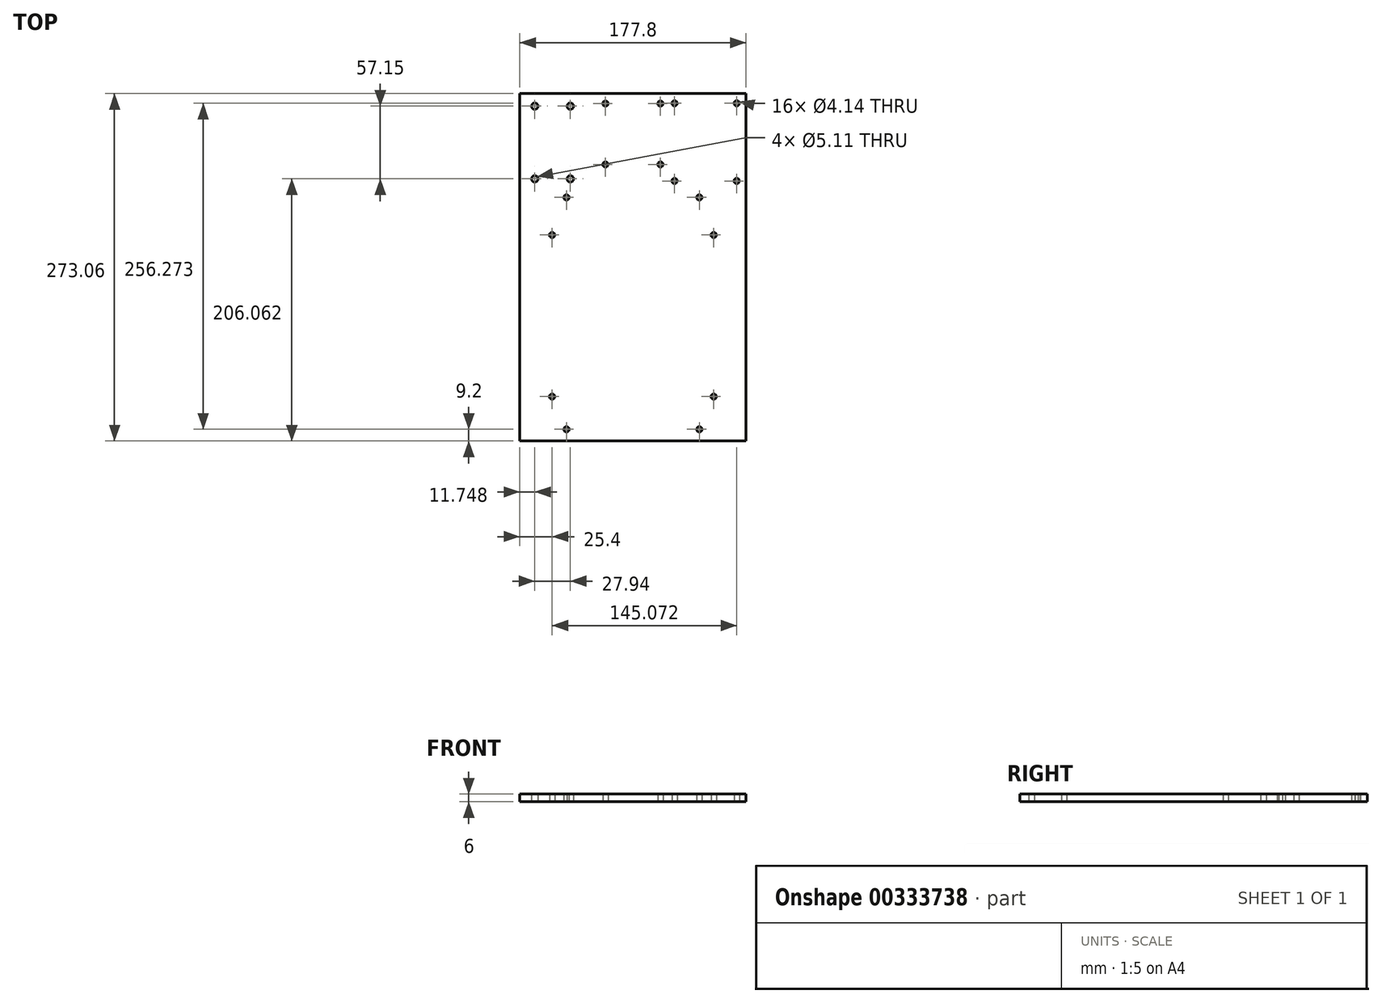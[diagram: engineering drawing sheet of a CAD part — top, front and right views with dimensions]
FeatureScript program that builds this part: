
annotation { "Feature Type Name" : "Feature", "Feature Type Description" : "" }
export const myFeature = defineFeature(function(context is Context, id is Id, definition is map)
    precondition{}
    {
        {
            var Q0;
            Q0=qCreatedBy(makeId("Top.planeOp"),FACE);
            var sketch = newSketch(context, id + "F0", { "sketchPlane" : qUnion([Q0])});
            skLineSegment(sketch, "E0.bottom", {"start": v(88.9, 136.52) * mm, "end": v(-88.9, 136.52) * mm});
            skLineSegment(sketch, "E0.top", {"start": v(88.9, -136.52) * mm, "end": v(-88.9, -136.52) * mm});
            skLineSegment(sketch, "E0.left", {"start": v(88.9, 136.52) * mm, "end": v(88.9, -136.52) * mm});
            skLineSegment(sketch, "E0.right", {"start": v(-88.9, 136.52) * mm, "end": v(-88.9, -136.52) * mm});
            skPoint(sketch, "E0.middle", {"position": v(0, 0) * mm});
            skLineSegment(sketch, "E1.bottom", {"start": v(71.59, 35.1) * mm, "end": v(-71.59, 35.1) * mm});
            skLineSegment(sketch, "E1.top", {"start": v(71.59, -111.3) * mm, "end": v(-71.59, -111.3) * mm, "construction": true});
            skLineSegment(sketch, "E1.left", {"start": v(71.59, 35.1) * mm, "end": v(71.59, -111.3) * mm, "construction": true});
            skLineSegment(sketch, "E1.right", {"start": v(-71.59, 35.1) * mm, "end": v(-71.59, -111.3) * mm, "construction": true});
            skPoint(sketch, "E1.middle", {"position": v(0, -38.1) * mm});
            skLineSegment(sketch, "E2.bottom", {"start": v(25.78, 76.58) * mm, "end": v(-25.78, 76.58) * mm});
            skLineSegment(sketch, "E2.top", {"start": v(25.78, 132.97) * mm, "end": v(-25.78, 132.97) * mm, "construction": true});
            skLineSegment(sketch, "E2.left", {"start": v(25.78, 76.58) * mm, "end": v(25.78, 132.97) * mm, "construction": true});
            skLineSegment(sketch, "E2.right", {"start": v(-25.78, 76.58) * mm, "end": v(-25.78, 132.97) * mm, "construction": true});
            skPoint(sketch, "E2.middle", {"position": v(0, 104.77) * mm});
            skLineSegment(sketch, "E3.bottom", {"start": v(21.62, 80.86) * mm, "end": v(-21.62, 80.86) * mm, "construction": true});
            skLineSegment(sketch, "E3.top", {"start": v(21.62, 128.69) * mm, "end": v(-21.62, 128.69) * mm, "construction": true});
            skLineSegment(sketch, "E3.left", {"start": v(21.62, 80.86) * mm, "end": v(21.62, 128.69) * mm, "construction": true});
            skLineSegment(sketch, "E3.right", {"start": v(-21.62, 80.86) * mm, "end": v(-21.62, 128.69) * mm, "construction": true});
            skLineSegment(sketch, "E4.bottom", {"start": v(85.55, 63.88) * mm, "end": v(28.75, 63.88) * mm, "construction": true});
            skLineSegment(sketch, "E4.top", {"start": v(85.55, 132.97) * mm, "end": v(28.75, 132.97) * mm, "construction": true});
            skLineSegment(sketch, "E4.left", {"start": v(85.55, 63.88) * mm, "end": v(85.55, 132.97) * mm, "construction": true});
            skLineSegment(sketch, "E4.right", {"start": v(28.75, 63.88) * mm, "end": v(28.75, 132.97) * mm, "construction": true});
            skPoint(sketch, "E4.middle", {"position": v(57.15, 98.42) * mm});
            skLineSegment(sketch, "E5.bottom", {"start": v(81.57, 67.9) * mm, "end": v(32.73, 67.9) * mm, "construction": true});
            skLineSegment(sketch, "E5.top", {"start": v(81.57, 128.94) * mm, "end": v(32.73, 128.94) * mm, "construction": true});
            skLineSegment(sketch, "E5.left", {"start": v(81.57, 67.9) * mm, "end": v(81.57, 128.94) * mm, "construction": true});
            skLineSegment(sketch, "E5.right", {"start": v(32.73, 67.9) * mm, "end": v(32.73, 128.94) * mm, "construction": true});
            skLineSegment(sketch, "E6.bottom", {"start": v(-63.5, -101.6) * mm, "end": v(63.5, -101.6) * mm, "construction": true});
            skLineSegment(sketch, "E6.top", {"start": v(-63.5, 25.4) * mm, "end": v(63.5, 25.4) * mm, "construction": true});
            skLineSegment(sketch, "E6.left", {"start": v(-63.5, -101.6) * mm, "end": v(-63.5, 25.4) * mm, "construction": true});
            skLineSegment(sketch, "E6.right", {"start": v(63.5, -101.6) * mm, "end": v(63.5, 25.4) * mm, "construction": true});
            skCircle(sketch, "E7", {"center": v(63.5, 25.4) * mm, "radius": 2.07 * mm});
            skCircle(sketch, "E8", {"center": v(-63.5, 25.4) * mm, "radius": 2.07 * mm});
            skCircle(sketch, "E9", {"center": v(-63.5, -101.6) * mm, "radius": 2.07 * mm});
            skCircle(sketch, "E10", {"center": v(63.5, -101.6) * mm, "radius": 2.07 * mm});
            skLineSegment(sketch, "E11.bottom", {"start": v(52.2, -127.33) * mm, "end": v(-52.2, -127.33) * mm, "construction": true});
            skLineSegment(sketch, "E11.top", {"start": v(52.2, 54.94) * mm, "end": v(-52.2, 54.94) * mm, "construction": true});
            skLineSegment(sketch, "E11.left", {"start": v(52.2, -127.33) * mm, "end": v(52.2, 54.94) * mm, "construction": true});
            skLineSegment(sketch, "E11.right", {"start": v(-52.2, -127.33) * mm, "end": v(-52.2, 54.94) * mm, "construction": true});
            skPoint(sketch, "E11.middle", {"position": v(0, -36.2) * mm});
            skCircle(sketch, "E12", {"center": v(32.73, 67.9) * mm, "radius": 2.07 * mm});
            skCircle(sketch, "E13", {"center": v(81.57, 67.9) * mm, "radius": 2.07 * mm});
            skCircle(sketch, "E14", {"center": v(81.57, 128.94) * mm, "radius": 2.07 * mm});
            skCircle(sketch, "E15", {"center": v(32.73, 128.94) * mm, "radius": 2.07 * mm});
            skCircle(sketch, "E16", {"center": v(21.62, 128.69) * mm, "radius": 2.07 * mm});
            skCircle(sketch, "E17", {"center": v(-21.62, 128.69) * mm, "radius": 2.07 * mm});
            skCircle(sketch, "E18", {"center": v(-21.62, 80.86) * mm, "radius": 2.07 * mm});
            skCircle(sketch, "E19", {"center": v(21.62, 80.86) * mm, "radius": 2.07 * mm});
            skCircle(sketch, "E20", {"center": v(52.2, -127.33) * mm, "radius": 2.07 * mm});
            skCircle(sketch, "E21", {"center": v(-52.2, -127.33) * mm, "radius": 2.07 * mm});
            skCircle(sketch, "E22", {"center": v(-52.2, 54.94) * mm, "radius": 2.07 * mm});
            skCircle(sketch, "E23", {"center": v(52.2, 54.94) * mm, "radius": 2.07 * mm});
            skLineSegment(sketch, "E24.bottom", {"start": v(57.4, -132.54) * mm, "end": v(-57.4, -132.54) * mm, "construction": true});
            skLineSegment(sketch, "E24.top", {"start": v(57.4, 60.15) * mm, "end": v(-57.4, 60.15) * mm, "construction": true});
            skLineSegment(sketch, "E24.left", {"start": v(57.4, -132.54) * mm, "end": v(57.4, 60.15) * mm, "construction": true});
            skLineSegment(sketch, "E24.right", {"start": v(-57.4, -132.54) * mm, "end": v(-57.4, 60.15) * mm, "construction": true});
            skLineSegment(sketch, "E25.bottom", {"start": v(-87.31, 134.94) * mm, "end": v(-39.05, 134.94) * mm, "construction": true});
            skLineSegment(sketch, "E25.top", {"start": v(-87.31, 61.28) * mm, "end": v(-39.05, 61.28) * mm, "construction": true});
            skLineSegment(sketch, "E25.left", {"start": v(-87.31, 134.94) * mm, "end": v(-87.31, 61.28) * mm, "construction": true});
            skLineSegment(sketch, "E25.right", {"start": v(-39.05, 134.94) * mm, "end": v(-39.05, 61.28) * mm, "construction": true});
            skLineSegment(sketch, "E26", {"start": v(-87.31, 134.94) * mm, "end": v(-39.05, 61.28) * mm, "construction": true});
            skLineSegment(sketch, "E27", {"start": v(-39.05, 134.94) * mm, "end": v(-87.31, 61.28) * mm, "construction": true});
            skPoint(sketch, "E28", {"position": v(-63.18, 98.1) * mm});
            skLineSegment(sketch, "E29.bottom", {"start": v(-49.21, 126.68) * mm, "end": v(-77.15, 126.68) * mm, "construction": true});
            skLineSegment(sketch, "E29.top", {"start": v(-49.21, 69.53) * mm, "end": v(-77.15, 69.53) * mm, "construction": true});
            skLineSegment(sketch, "E29.left", {"start": v(-49.21, 126.68) * mm, "end": v(-49.21, 69.53) * mm, "construction": true});
            skLineSegment(sketch, "E29.right", {"start": v(-77.15, 126.68) * mm, "end": v(-77.15, 69.53) * mm, "construction": true});
            skCircle(sketch, "E30", {"center": v(-77.15, 126.68) * mm, "radius": 2.55 * mm});
            skCircle(sketch, "E31", {"center": v(-49.21, 126.68) * mm, "radius": 2.55 * mm});
            skCircle(sketch, "E32", {"center": v(-49.21, 69.53) * mm, "radius": 2.55 * mm});
            skCircle(sketch, "E33", {"center": v(-77.15, 69.53) * mm, "radius": 2.55 * mm});
            skSolve(sketch);
        }
        {
            var Q0;
            Q0=makeQuery(id+"F0.imprint","IMPRINT",FACE,{"disambiguationData":[TD([[makeQuery(id+"F0.imprint","IMPRINT",EDGE,{"derivedFrom":sQuery(id+"F0.wireOp",EDGE,"E0.bottom")}),1.0]])]});
            extrude(context, id + "F1", {"entities" : qUnion([Q0]), "depth" : 6 * mm});
        }
    });
